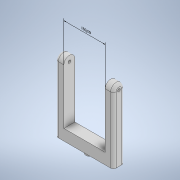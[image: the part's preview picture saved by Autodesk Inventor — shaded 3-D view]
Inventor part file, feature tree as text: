
AUTODESK INVENTOR PART (.ipt)
format: ipt  version: 2021 (Build 250183000, 183)  size: 171,008 bytes
history: native  units: mm
features: extrude x6, sketch x6, other x2, fillet x1
ambient origin geometry x8: Origin, YZ Plane, XZ Plane, XY Plane, X Axis, Y Axis, Z Axis, Center Point
bodies: Solid1 (feature_tree)
feature tree (15):
  other  "Annotations"
  extrude  "Extrusion1"  Depth=40.0mm
  extrude  "Extrusion2"  Depth=40.0mm
  extrude  "Extrusion3"  Depth=30.0mm
  extrude  "Extrusion4"  Depth=30.0mm TaperAngle=0.0deg
  extrude  "Extrusion5"  Depth=10.0mm TaperAngle=0.0deg
  fillet  "Fillet1"  Radius=10.0mm
  extrude  "Extrusion6"  TaperAngle=0.0deg  [1 undecoded]
  sketch  "Sketch1"  dims[d0=20.0mm d1=40.0mm]
  sketch  "Sketch2"  dims[d2=40.0mm d3=40.0mm]
  sketch  "Sketch3"  dims[d4=210.0mm d5=0.0mm d6=30.0mm]
  sketch  "Sketch4"  dims[d7=30.0mm d8=200.0mm d9=0.0mm]
  sketch  "Sketch5"  dims[d10=200.0mm d11=0.0mm d12=200.0mm d13=0.0mm d14=10.0mm]
  sketch  "Sketch6"  dims[d15=10.0mm d16=0.0mm d17=0.0mm d20=10.0mm d21=30.0mm d22=10.0mm d23=0.0mm d18=8.345735mm d19=150.0mm]
  other  "Linear Dimension 1"
note: 1 required parameter value undecoded (feature->parameter linkage not recoverable at this tier; creation-order binding heuristic only, values carry confidence <= 0.55)
